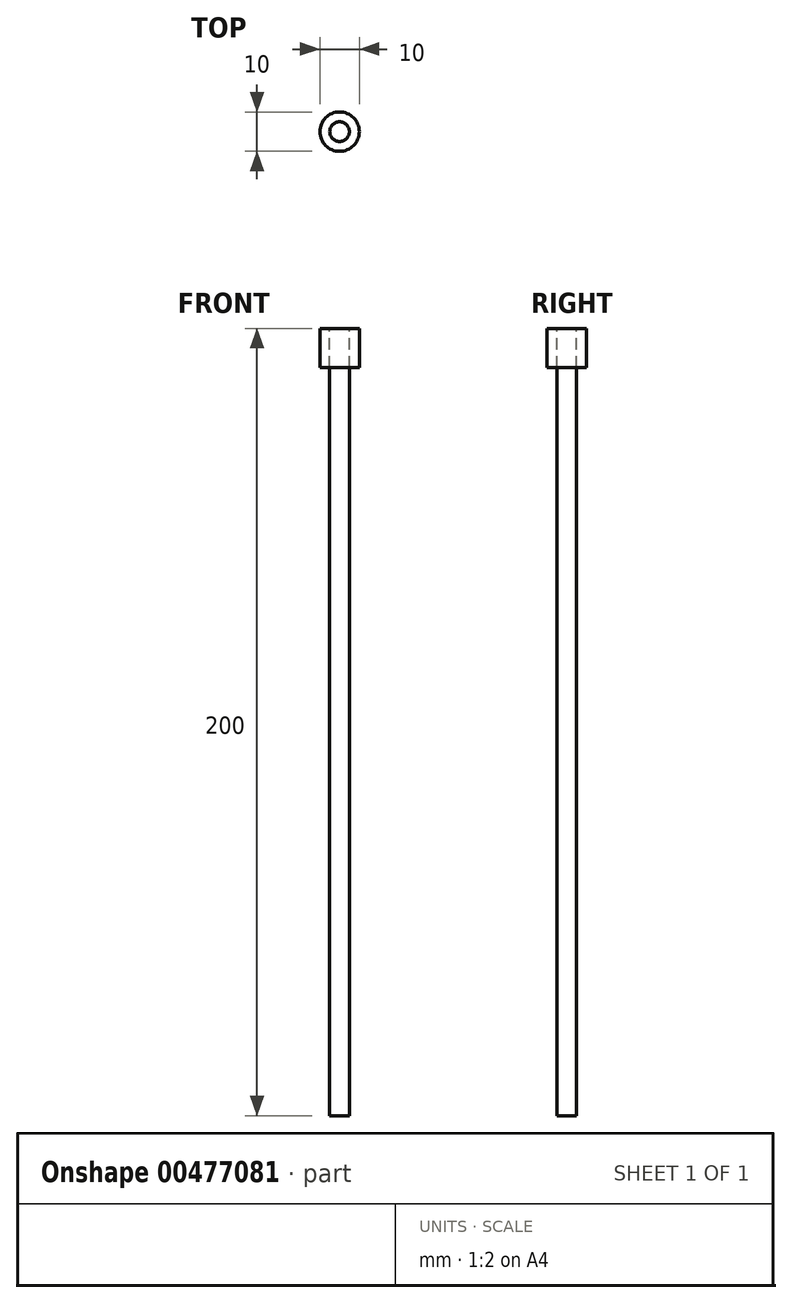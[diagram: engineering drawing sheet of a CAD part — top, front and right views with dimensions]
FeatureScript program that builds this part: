
annotation { "Feature Type Name" : "Feature", "Feature Type Description" : "" }
export const myFeature = defineFeature(function(context is Context, id is Id, definition is map)
    precondition{}
    {
        {
            var Q0;
            Q0=qCreatedBy(makeId("Top.planeOp"),FACE);
            var sketch = newSketch(context, id + "F0", { "sketchPlane" : qUnion([Q0])});
            skCircle(sketch, "E0", {"center": v(0, 0) * mm, "radius": 2.5 * mm});
            skSolve(sketch);
        }
        {
            var Q0;
            Q0=qCreatedBy(makeId("Top.planeOp"),FACE);
            var sketch = newSketch(context, id + "F1", { "sketchPlane" : qUnion([Q0])});
            skCircle(sketch, "E1", {"center": v(0, 0) * mm, "radius": 5 * mm});
            skSolve(sketch);
        }
        {
            var Q0;
            Q0 = qSketchRegion(id + "F1", true);
            extrude(context, id + "F2", {"entities" : qUnion([Q0]), "oppositeDirection" : true, "depth" : 10 * mm, "offsetDistance" : 25 * mm});
        }
        {
            var Q0;
            Q0 = qSketchRegion(id + "F0", true);
            extrude(context, id + "F3", {"entities" : qUnion([Q0]), "oppositeDirection" : true, "depth" : 200 * mm, "offsetDistance" : 25 * mm});
        }
    });
